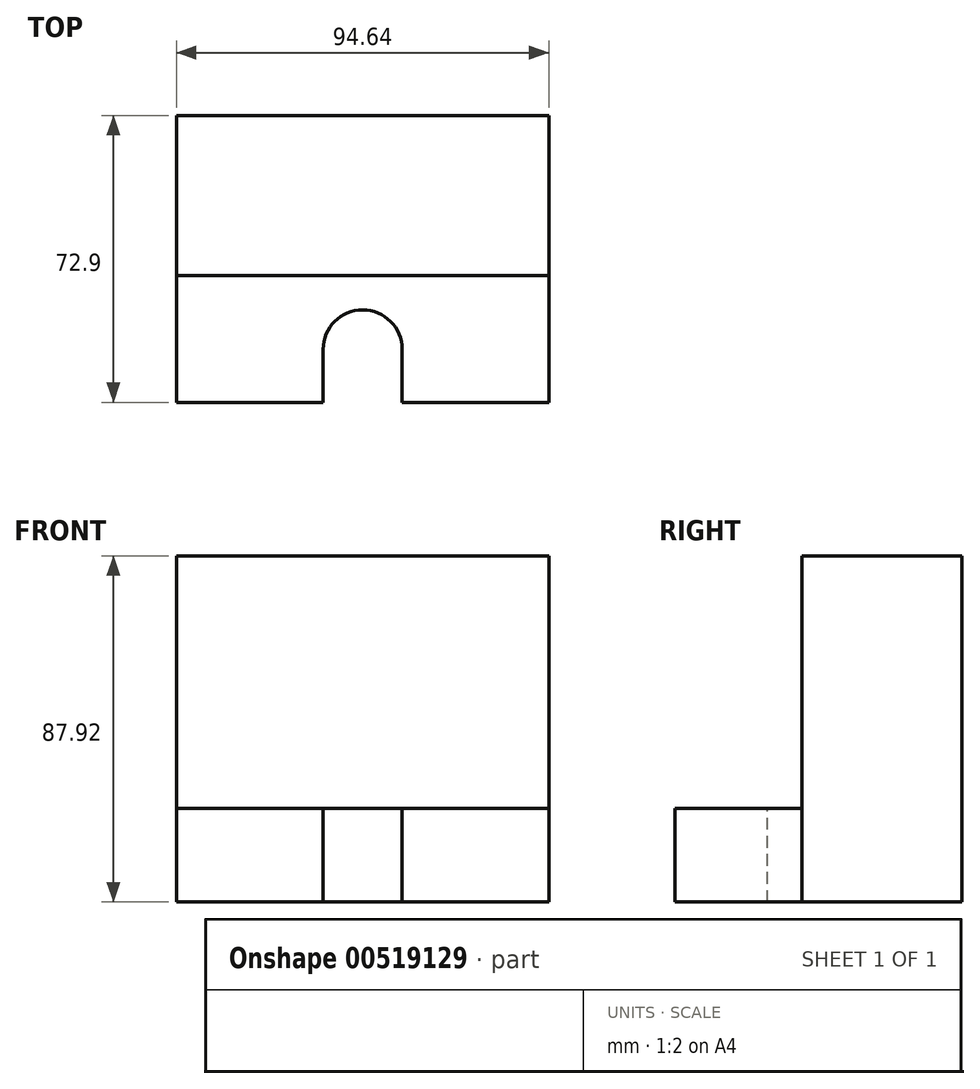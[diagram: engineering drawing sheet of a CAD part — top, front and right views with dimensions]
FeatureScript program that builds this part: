
annotation { "Feature Type Name" : "Feature", "Feature Type Description" : "" }
export const myFeature = defineFeature(function(context is Context, id is Id, definition is map)
    precondition{}
    {
        {
            var Q0;
            Q0=qCreatedBy(makeId("Front.planeOp"),FACE);
            var sketch = newSketch(context, id + "F0", { "sketchPlane" : qUnion([Q0])});
            skLineSegment(sketch, "E0.bottom", {"start": v(47.32, 43.96) * mm, "end": v(-47.32, 43.96) * mm});
            skLineSegment(sketch, "E0.top", {"start": v(47.32, -43.96) * mm, "end": v(-47.32, -43.96) * mm});
            skLineSegment(sketch, "E0.left", {"start": v(47.32, 43.96) * mm, "end": v(47.32, -43.96) * mm});
            skLineSegment(sketch, "E0.right", {"start": v(-47.32, 43.96) * mm, "end": v(-47.32, -43.96) * mm});
            skPoint(sketch, "E0.middle", {"position": v(0, 0) * mm});
            skSolve(sketch);
        }
        {
            var Q0;
            Q0=makeQuery(id+"F0.imprint","IMPRINT",FACE,{"disambiguationData":[TD([[makeQuery(id+"F0.imprint","IMPRINT",EDGE,{"derivedFrom":sQuery(id+"F0.wireOp",EDGE,"E0.bottom")}),1.0]])]});
            extrude(context, id + "F1", {"entities" : qUnion([Q0]), "endBound" : BoundingType.SYMMETRIC, "depth" : 40.64 * mm, "offsetDistance" : 25.4 * mm});
        }
        {
            var Q0;
            Q0=makeQuery(id+"F1.opExtrude","CAP_FACE",FACE,{"disambiguationData":[OSD([sQuery(id+"F0.wireOp",EDGE,"E0.bottom"),sQuery(id+"F0.wireOp",EDGE,"E0.top"),sQuery(id+"F0.wireOp",EDGE,"E0.left"),sQuery(id+"F0.wireOp",EDGE,"E0.right")])],"isStart":false});
            var sketch = newSketch(context, id + "F2", { "sketchPlane" : qUnion([Q0])});
            skLineSegment(sketch, "E1.bottom", {"start": v(47.32, -43.96) * mm, "end": v(-47.32, -43.96) * mm});
            skLineSegment(sketch, "E1.top", {"start": v(47.32, -20.15) * mm, "end": v(-47.32, -20.15) * mm});
            skLineSegment(sketch, "E1.left", {"start": v(47.32, -43.96) * mm, "end": v(47.32, -20.15) * mm});
            skLineSegment(sketch, "E1.right", {"start": v(-47.32, -43.96) * mm, "end": v(-47.32, -20.15) * mm});
            skPoint(sketch, "E1.middle", {"position": v(0, -32.05) * mm});
            skSolve(sketch);
        }
        {
            var Q0;
            Q0=makeQuery(id+"F2.imprint","IMPRINT",FACE,{"disambiguationData":[TD([[makeQuery(id+"F2.imprint","IMPRINT",EDGE,{"derivedFrom":sQuery(id+"F2.wireOp",EDGE,"E1.bottom")}),-1.0]])]});
            extrude(context, id + "F3", {"entities" : qUnion([Q0]), "depth" : 32.26 * mm, "offsetDistance" : 25.4 * mm});
        }
        {
            var Q0;
            Q0=makeQuery(id+"F3.opExtrude","SWEPT_FACE",FACE,{"disambiguationData":[OSD([sQuery(id+"F2.wireOp",EDGE,"E1.top")])]});
            var sketch = newSketch(context, id + "F4", { "sketchPlane" : qUnion([Q0])});
            skCircle(sketch, "E2", {"center": v(0, -39.07) * mm, "radius": 10.03 * mm});
            skLineSegment(sketch, "E3", {"start": v(-10.03, -39.07) * mm, "end": v(-10.03, -52.58) * mm});
            skLineSegment(sketch, "E4", {"start": v(10.03, -39.07) * mm, "end": v(10.03, -52.58) * mm});
            skPoint(sketch, "E5", {"position": v(0, -52.58) * mm});
            skSolve(sketch);
        }
        {
            var Q0;
            {var subQ0=sQuery(id+"F4.wireOp",EDGE,"E2");var subQ1=makeQuery(id+"F4.imprint","INTERSECT",VERTEX,{"derivedFrom":[subQ0,sQuery(id+"F4.wireOp",EDGE,"E3")]});Q0=makeQuery(id+"F4.imprint","IMPRINT",FACE,{"disambiguationData":[TD([[makeQuery(id+"F4.imprint","IMPRINT",EDGE,{"disambiguationData":[TD([[subQ1,-1.0]])],"derivedFrom":subQ0}),1.0]])]});}
            var Q1;
            {var subQ0=sQuery(id+"F4.wireOp",EDGE,"E3");Q1=makeQuery(id+"F4.imprint","IMPRINT",FACE,{"disambiguationData":[TD([[makeQuery(id+"F4.imprint","IMPRINT",EDGE,{"derivedFrom":subQ0}),1.0]])]});}
            extrude(context, id + "F5", {"entities" : qUnion([Q0, Q1]), "operationType" : NewBodyOperationType.REMOVE, "endBound" : BoundingType.THROUGH_ALL, "oppositeDirection" : true, "depth" : 25.4 * mm, "offsetDistance" : 25.4 * mm});
        }
    });
